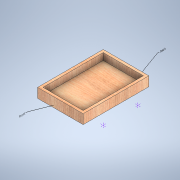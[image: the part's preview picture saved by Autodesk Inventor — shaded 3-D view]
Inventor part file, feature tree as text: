
AUTODESK INVENTOR PART (.ipt)
format: ipt  version: 2020 (Build 240168000, 168)  size: 124,416 bytes
history: native  units: in
note: dims shown in document units (in); Inventor stores cm internally (conversion verified against a paired STEP export)
features: other x3, sketch x2, extrude x1, shell x1
ambient origin geometry x8: Origin, YZ Plane, XZ Plane, XY Plane, X Axis, Y Axis, Z Axis, Center Point
bodies: Solid1 (feature_tree)
feature tree (7):
  other  "Annotations"
  extrude  "Extrusion1"  Depth=14.1732in
  shell  "Shell1"  Thickness=2.0472in
  sketch  "3D Sketch5"
  sketch  "Sketch1"  dims[d0=9.8425in d1=14.1732in d2=2.0472in d3=0.0in d4=0.5906in d5=0.1354in d6=0.0742in d7=0.0893in d8=0.1577in]
  other  "Leader Text 1"
  other  "Leader Text 2"
